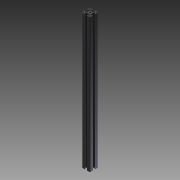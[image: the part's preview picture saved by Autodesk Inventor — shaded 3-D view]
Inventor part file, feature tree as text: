
AUTODESK INVENTOR PART (.ipt)
format: ipt  version: 2011 SP1 (Build 150282100, 282)  size: 186,368 bytes
history: native  units: mm
features: other x21, sketch x3, hole x2, extrude x1, pattern_linear x1
ambient origin geometry x8: Origin, YZ Plane, XZ Plane, XY Plane, X Axis, Y Axis, Z Axis, Center Point
bodies: Solid1 (feature_tree)
feature tree (28):
  extrude  "Extrusion1"  Depth=20.0mm
  hole  "Hole1"  [1 undecoded]
  hole  "Hole2"  [1 undecoded]
  pattern_linear  "Rectangular Pattern1"  [2 undecoded]
  other  "C1_XY"
  other  "C1_YZ"
  other  "C1_ZX"
  other  "C1_X"
  other  "C1_Y"
  other  "C1_Z"
  other  "C1_Center"
  other  "to_frame_cap1_XY"
  other  "to_frame_cap1_YZ"
  other  "to_frame_cap1_ZX"
  other  "to_frame_cap1_X"
  other  "to_frame_cap1_Y"
  other  "to_frame_cap1_Z"
  other  "to_frame_cap1_Center"
  other  "to_frame_cap2_XY"
  other  "to_frame_cap2_YZ"
  other  "to_frame_cap2_ZX"
  other  "to_frame_cap2_X"
  other  "to_frame_cap2_Y"
  other  "to_frame_cap2_Z"
  other  "to_frame_cap2_Center"
  sketch  "Sketch_1"  dims[d0=500.0mm d1=0.0mm]
  sketch  "Sketch2"  dims[d2=6.8mm d3=6.0mm d4=4.0mm d5=2.0mm d6=90.0deg d7=500.0mm d8=0.0mm]
  sketch  "Sketch3"  dims[d9=4.2mm d10=6.0mm d11=4.0mm d12=2.0mm d13=90.0deg d14=500.0mm d15=0.0mm d16=20.0mm d18=23.2mm d19=20.0mm d21=23.2mm d22=0.0mm d23=0.0mm d24=0.0mm]
note: 4 required parameter values undecoded (feature->parameter linkage not recoverable at this tier; creation-order binding heuristic only, values carry confidence <= 0.55)
